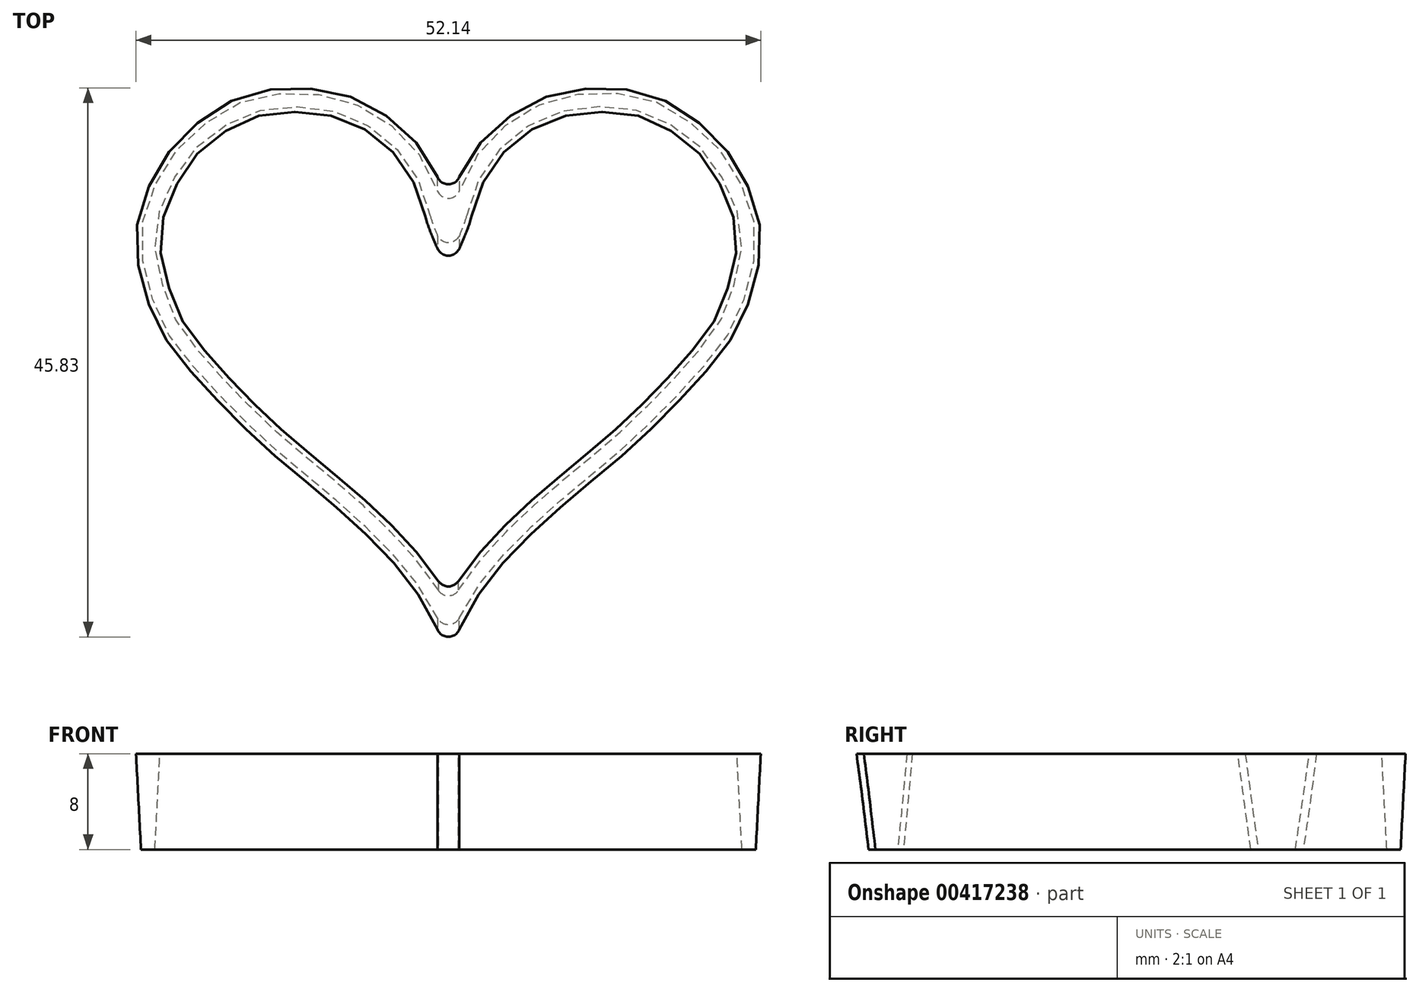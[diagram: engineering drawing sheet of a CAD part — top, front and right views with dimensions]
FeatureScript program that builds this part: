
annotation { "Feature Type Name" : "Feature", "Feature Type Description" : "" }
export const myFeature = defineFeature(function(context is Context, id is Id, definition is map)
    precondition{}
    {
        {
            var Q0;
            Q0=qCreatedBy(makeId("Top.planeOp"),FACE);
            var sketch = newSketch(context, id + "F0", { "sketchPlane" : qUnion([Q0])});
            skLineSegment(sketch, "E0", {"start": v(0, 0) * mm, "end": v(-23.1, 0) * mm, "construction": true});
            skLineSegment(sketch, "E1", {"start": v(0, 0) * mm, "end": v(0, 9) * mm, "construction": true});
            skLineSegment(sketch, "E2", {"start": v(0, 0) * mm, "end": v(0, -25.53) * mm, "construction": true});
            skFitSpline(sketch, "E3", {"points": [v(0, -25.53) * mm, v(-3.22, -19.63) * mm, v(-10.62, -12.4) * mm, v(-15.3, -8.43) * mm, v(-23.1, 0) * mm, v(-24.8, 3.68) * mm, v(-25.64, 8.82) * mm, v(-23.84, 14.09) * mm, v(-21.76, 16.76) * mm, v(-17.5, 19.71) * mm, v(-13.07, 20.55) * mm, v(-8.64, 19.95) * mm, v(-4.57, 17.68) * mm, v(-1.58, 13.97) * mm, v(0, 9) * mm], "startDerivative": vector(-21.33, 67.93) * mm, "endDerivative": vector(17.09, -71.8) * mm});
            skFitSpline(sketch, "E4.MirrorCS", {"points": [v(0, -25.53) * mm, v(3.22, -19.63) * mm, v(10.62, -12.4) * mm, v(15.3, -8.43) * mm, v(23.1, 0) * mm, v(24.8, 3.68) * mm, v(25.64, 8.82) * mm, v(23.84, 14.09) * mm, v(21.76, 16.76) * mm, v(17.5, 19.71) * mm, v(13.07, 20.55) * mm, v(8.64, 19.95) * mm, v(4.57, 17.68) * mm, v(1.58, 13.97) * mm, v(0, 9) * mm], "startDerivative": vector(21.33, 67.93) * mm, "endDerivative": vector(-17.09, -71.8) * mm});
            skSolve(sketch);
        }
        {
            var Q0;
            Q0 = qSketchRegion(id + "F0", true);
            extrude(context, id + "F1", {"entities" : qUnion([Q0]), "depth" : 8 * mm, "hasDraft" : true, "draftAngle" : 3 * degree});
        }
        {
            var Q0;
            Q0=makeQuery(id+"F1.opExtrude","CAP_FACE",FACE,{"disambiguationData":[OSD([sQuery(id+"F0.wireOp",EDGE,"E3"),sQuery(id+"F0.wireOp",EDGE,"E4.MirrorCS")])],"isStart":false});
            var sketch = newSketch(context, id + "F2", { "sketchPlane" : qUnion([Q0])});
            skFitSpline(sketch, "E5.1", {"points": [v(0, -26.93) * mm, v(-0.13, -26.5) * mm, v(-0.27, -26.08) * mm, v(-0.4, -25.65) * mm, v(-0.83, -24.28) * mm, v(-1.54, -22.73) * mm, v(-2.94, -20.7) * mm, v(-3.24, -20.28) * mm, v(-3.9, -19.45) * mm, v(-4.26, -19.02) * mm, v(-5.4, -17.76) * mm, v(-6.23, -16.91) * mm, v(-7.92, -15.3) * mm, v(-8.77, -14.53) * mm, v(-9.97, -13.5) * mm, v(-10.36, -13.16) * mm, v(-11.09, -12.55) * mm, v(-11.43, -12.27) * mm, v(-12.4, -11.47) * mm, v(-13, -11) * mm, v(-14.26, -9.94) * mm, v(-14.92, -9.36) * mm, v(-17.24, -7.21) * mm, v(-19.2, -5.25) * mm, v(-21.72, -2.45) * mm, v(-22.48, -1.54) * mm, v(-23.23, -0.53) * mm, v(-23.38, -0.34) * mm, v(-23.63, 0.04) * mm, v(-23.75, 0.22) * mm, v(-24.08, 0.75) * mm, v(-24.26, 1.08) * mm, v(-24.56, 1.72) * mm, v(-24.7, 2.02) * mm, v(-24.92, 2.64) * mm, v(-25.02, 2.95) * mm, v(-25.17, 3.44) * mm, v(-25.22, 3.6) * mm, v(-25.32, 3.94) * mm, v(-25.37, 4.12) * mm, v(-25.53, 4.66) * mm, v(-25.63, 5.04) * mm, v(-25.9, 6.23) * mm, v(-26.05, 7.09) * mm, v(-26.08, 8.18) * mm, v(-26.08, 8.4) * mm, v(-26.06, 8.85) * mm, v(-26.04, 9.07) * mm, v(-25.96, 9.74) * mm, v(-25.87, 10.17) * mm, v(-25.53, 11.46) * mm, v(-25.2, 12.28) * mm, v(-24.68, 13.4) * mm, v(-24.5, 13.76) * mm, v(-24.14, 14.43) * mm, v(-23.96, 14.74) * mm, v(-23.42, 15.61) * mm, v(-23.04, 16.13) * mm, v(-22.36, 16.89) * mm, v(-22.12, 17.14) * mm, v(-21.58, 17.64) * mm, v(-21.28, 17.88) * mm, v(-20.35, 18.62) * mm, v(-19.65, 19.09) * mm, v(-18.56, 19.7) * mm, v(-18.19, 19.88) * mm, v(-17.44, 20.2) * mm, v(-17.07, 20.33) * mm, v(-15.94, 20.68) * mm, v(-15.2, 20.82) * mm, v(-14.07, 20.93) * mm, v(-13.7, 20.95) * mm, v(-12.95, 20.98) * mm, v(-12.57, 20.98) * mm, v(-11.44, 20.94) * mm, v(-10.68, 20.86) * mm, v(-9.56, 20.64) * mm, v(-9.19, 20.55) * mm, v(-8.45, 20.34) * mm, v(-8.08, 20.21) * mm, v(-7, 19.77) * mm, v(-6.31, 19.4) * mm, v(-5, 18.57) * mm, v(-4.37, 18.09) * mm, v(-3.22, 17.03) * mm, v(-2.69, 16.45) * mm, v(-1.98, 15.49) * mm, v(-1.76, 15.16) * mm, v(-1.36, 14.46) * mm, v(-1.17, 14.1) * mm, v(-0.67, 12.99) * mm, v(-0.4, 12.2) * mm, v(-0.12, 11.2) * mm, v(-0.06, 10.97) * mm, v(0, 10.75) * mm], "construction": true});
            skFitSpline(sketch, "E6.0", {"points": [v(0, -26.93) * mm, v(0.13, -26.5) * mm, v(0.27, -26.08) * mm, v(0.4, -25.65) * mm, v(0.83, -24.28) * mm, v(1.54, -22.73) * mm, v(2.94, -20.7) * mm, v(3.24, -20.28) * mm, v(3.9, -19.45) * mm, v(4.26, -19.02) * mm, v(5.4, -17.76) * mm, v(6.23, -16.91) * mm, v(7.92, -15.3) * mm, v(8.77, -14.53) * mm, v(9.97, -13.5) * mm, v(10.36, -13.16) * mm, v(11.09, -12.55) * mm, v(11.43, -12.27) * mm, v(12.4, -11.47) * mm, v(13, -11) * mm, v(14.26, -9.94) * mm, v(14.92, -9.36) * mm, v(17.24, -7.21) * mm, v(19.2, -5.25) * mm, v(21.72, -2.45) * mm, v(22.48, -1.54) * mm, v(23.23, -0.53) * mm, v(23.38, -0.34) * mm, v(23.63, 0.04) * mm, v(23.75, 0.22) * mm, v(24.08, 0.75) * mm, v(24.26, 1.08) * mm, v(24.56, 1.72) * mm, v(24.7, 2.02) * mm, v(24.92, 2.64) * mm, v(25.02, 2.95) * mm, v(25.17, 3.44) * mm, v(25.22, 3.6) * mm, v(25.32, 3.94) * mm, v(25.37, 4.12) * mm, v(25.53, 4.66) * mm, v(25.63, 5.04) * mm, v(25.9, 6.23) * mm, v(26.05, 7.09) * mm, v(26.08, 8.18) * mm, v(26.08, 8.4) * mm, v(26.06, 8.85) * mm, v(26.04, 9.07) * mm, v(25.96, 9.74) * mm, v(25.87, 10.17) * mm, v(25.53, 11.46) * mm, v(25.2, 12.28) * mm, v(24.68, 13.4) * mm, v(24.5, 13.76) * mm, v(24.14, 14.43) * mm, v(23.96, 14.74) * mm, v(23.42, 15.61) * mm, v(23.04, 16.13) * mm, v(22.36, 16.89) * mm, v(22.12, 17.14) * mm, v(21.58, 17.64) * mm, v(21.28, 17.88) * mm, v(20.35, 18.62) * mm, v(19.65, 19.09) * mm, v(18.56, 19.7) * mm, v(18.19, 19.88) * mm, v(17.44, 20.2) * mm, v(17.07, 20.33) * mm, v(15.94, 20.68) * mm, v(15.2, 20.82) * mm, v(14.07, 20.93) * mm, v(13.7, 20.95) * mm, v(12.95, 20.98) * mm, v(12.57, 20.98) * mm, v(11.44, 20.94) * mm, v(10.68, 20.86) * mm, v(9.56, 20.64) * mm, v(9.19, 20.55) * mm, v(8.45, 20.34) * mm, v(8.08, 20.21) * mm, v(7, 19.77) * mm, v(6.31, 19.4) * mm, v(5, 18.57) * mm, v(4.37, 18.09) * mm, v(3.22, 17.03) * mm, v(2.69, 16.45) * mm, v(1.98, 15.49) * mm, v(1.76, 15.16) * mm, v(1.36, 14.46) * mm, v(1.17, 14.1) * mm, v(0.67, 12.99) * mm, v(0.4, 12.2) * mm, v(0.12, 11.2) * mm, v(0.06, 10.97) * mm, v(0, 10.75) * mm], "construction": true});
            skFitSpline(sketch, "E7.0", {"points": [v(1.9, -26.33) * mm, v(1.85, -26.16) * mm, v(1.77, -25.9) * mm, v(1.67, -25.56) * mm, v(1.6, -25.34) * mm, v(1.55, -25.2) * mm, v(1.52, -25.1) * mm, v(1.5, -25.04) * mm, v(1.48, -24.97) * mm, v(1.45, -24.87) * mm, v(1.4, -24.7) * mm, v(1.3, -24.45) * mm, v(1.16, -24.05) * mm, v(0.96, -23.53) * mm, v(0.59, -22.7) * mm, v(0.04, -21.63) * mm, v(-0.76, -20.31) * mm, v(-1.7, -18.97) * mm, v(-2.83, -17.6) * mm, v(-4.46, -15.83) * mm, v(-6.23, -14.13) * mm, v(-7.94, -12.6) * mm, v(-8.95, -11.74) * mm, v(-9.7, -11.11) * mm, v(-10.39, -10.54) * mm, v(-11.19, -9.89) * mm, v(-12.09, -9.15) * mm, v(-13, -8.38) * mm, v(-13.82, -7.65) * mm, v(-14.56, -6.96) * mm, v(-15.36, -6.21) * mm, v(-16.42, -5.17) * mm, v(-17.74, -3.83) * mm, v(-19.04, -2.45) * mm, v(-20.03, -1.33) * mm, v(-20.74, -0.48) * mm, v(-21.23, 0.12) * mm, v(-21.65, 0.68) * mm, v(-22, 1.18) * mm, v(-22.27, 1.62) * mm, v(-22.57, 2.16) * mm, v(-22.79, 2.65) * mm, v(-22.98, 3.16) * mm, v(-23.11, 3.57) * mm, v(-23.25, 4.03) * mm, v(-23.45, 4.69) * mm, v(-23.7, 5.54) * mm, v(-23.94, 6.6) * mm, v(-24.06, 7.5) * mm, v(-24.08, 8.1) * mm, v(-24.08, 8.45) * mm, v(-24.06, 8.78) * mm, v(-24.01, 9.2) * mm, v(-23.88, 9.9) * mm, v(-23.62, 10.8) * mm, v(-23.2, 11.85) * mm, v(-22.85, 12.6) * mm, v(-22.6, 13.06) * mm, v(-22.44, 13.36) * mm, v(-22.16, 13.85) * mm, v(-21.78, 14.46) * mm, v(-21.3, 15.09) * mm, v(-20.75, 15.68) * mm, v(-20.05, 16.32) * mm, v(-19.21, 16.96) * mm, v(-18.3, 17.56) * mm, v(-17.52, 17.98) * mm, v(-16.9, 18.25) * mm, v(-16.3, 18.48) * mm, v(-15.23, 18.8) * mm, v(-13.98, 18.95) * mm, v(-12.65, 18.98) * mm, v(-11.33, 18.93) * mm, v(-10.04, 18.73) * mm, v(-8.83, 18.37) * mm, v(-7.64, 17.87) * mm, v(-6.5, 17.19) * mm, v(-5.45, 16.37) * mm, v(-4.72, 15.69) * mm, v(-4.07, 14.96) * mm, v(-3.5, 14.16) * mm, v(-3.08, 13.45) * mm, v(-2.8, 12.85) * mm, v(-2.53, 12.2) * mm, v(-2.24, 11.34) * mm, v(-2.03, 10.61) * mm, v(-1.93, 10.24) * mm]});
            skFitSpline(sketch, "E7.1", {"points": [v(-1.9, -26.33) * mm, v(-1.85, -26.16) * mm, v(-1.77, -25.9) * mm, v(-1.67, -25.56) * mm, v(-1.6, -25.34) * mm, v(-1.55, -25.2) * mm, v(-1.52, -25.1) * mm, v(-1.5, -25.04) * mm, v(-1.48, -24.97) * mm, v(-1.45, -24.87) * mm, v(-1.4, -24.7) * mm, v(-1.3, -24.45) * mm, v(-1.16, -24.05) * mm, v(-0.96, -23.53) * mm, v(-0.59, -22.7) * mm, v(-0.04, -21.63) * mm, v(0.76, -20.31) * mm, v(1.7, -18.97) * mm, v(2.83, -17.6) * mm, v(4.46, -15.83) * mm, v(6.23, -14.13) * mm, v(7.94, -12.6) * mm, v(8.95, -11.74) * mm, v(9.7, -11.11) * mm, v(10.39, -10.54) * mm, v(11.19, -9.89) * mm, v(12.09, -9.15) * mm, v(13, -8.38) * mm, v(13.82, -7.65) * mm, v(14.56, -6.96) * mm, v(15.36, -6.21) * mm, v(16.42, -5.17) * mm, v(17.74, -3.83) * mm, v(19.04, -2.45) * mm, v(20.03, -1.33) * mm, v(20.74, -0.48) * mm, v(21.23, 0.12) * mm, v(21.65, 0.68) * mm, v(22, 1.18) * mm, v(22.27, 1.62) * mm, v(22.57, 2.16) * mm, v(22.79, 2.65) * mm, v(22.98, 3.16) * mm, v(23.11, 3.57) * mm, v(23.25, 4.03) * mm, v(23.45, 4.69) * mm, v(23.7, 5.54) * mm, v(23.94, 6.6) * mm, v(24.06, 7.5) * mm, v(24.08, 8.1) * mm, v(24.08, 8.45) * mm, v(24.06, 8.78) * mm, v(24.01, 9.2) * mm, v(23.88, 9.9) * mm, v(23.62, 10.8) * mm, v(23.2, 11.85) * mm, v(22.85, 12.6) * mm, v(22.6, 13.06) * mm, v(22.44, 13.36) * mm, v(22.16, 13.85) * mm, v(21.78, 14.46) * mm, v(21.3, 15.09) * mm, v(20.75, 15.68) * mm, v(20.05, 16.32) * mm, v(19.21, 16.96) * mm, v(18.3, 17.56) * mm, v(17.52, 17.98) * mm, v(16.9, 18.25) * mm, v(16.3, 18.48) * mm, v(15.23, 18.8) * mm, v(13.98, 18.95) * mm, v(12.65, 18.98) * mm, v(11.33, 18.93) * mm, v(10.04, 18.73) * mm, v(8.83, 18.37) * mm, v(7.64, 17.87) * mm, v(6.5, 17.19) * mm, v(5.45, 16.37) * mm, v(4.72, 15.69) * mm, v(4.07, 14.96) * mm, v(3.5, 14.16) * mm, v(3.08, 13.45) * mm, v(2.8, 12.85) * mm, v(2.53, 12.2) * mm, v(2.24, 11.34) * mm, v(2.03, 10.61) * mm, v(1.93, 10.24) * mm]});
            skLineSegment(sketch, "E8", {"start": v(0, 0) * mm, "end": v(0, 10.75) * mm, "construction": true});
            skFitSpline(sketch, "E9", {"points": [v(-1.93, 10.24) * mm, v(0, 4.23) * mm], "startDerivative": vector(1.44, -5.47) * mm, "endDerivative": vector(0, -5.66) * mm});
            skFitSpline(sketch, "E10.MirrorCS", {"points": [v(1.93, 10.24) * mm, v(0, 4.23) * mm], "startDerivative": vector(-1.44, -5.47) * mm, "endDerivative": vector(0, -5.66) * mm});
            skSolve(sketch);
        }
        {
            var Q0;
            Q0 = qSketchRegion(id + "F2", true);
            extrude(context, id + "F3", {"entities" : qUnion([Q0]), "operationType" : NewBodyOperationType.REMOVE, "oppositeDirection" : true, "depth" : 25 * mm, "hasDraft" : true, "draftAngle" : 3 * degree});
        }
        {
            var Q0;
            Q0=makeQuery(id+"F3.boolean.opBoolean","COPY",EDGE,{"derivedFrom":makeQuery(id+"F3.opExtrude","SWEPT_EDGE",EDGE,{"disambiguationData":[OSD([sQuery(id+"F2.wireOp",EDGE,"E9"),sQuery(id+"F2.wireOp",EDGE,"E10.MirrorCS")])]})});
            var Q1;
            {var subQ0=sQuery(id+"F0.wireOp",EDGE,"E4.MirrorCS");var subQ1=sQuery(id+"F0.wireOp",EDGE,"E3");Q1=makeQuery(id+"F1.opExtrude","SWEPT_EDGE",EDGE,{"disambiguationData":[OSD([subQ1,subQ0]),TDD([makeQuery(id+"F0.imprint","INTERSECT",VERTEX,{"disambiguationData":[OD(1.0)],"derivedFrom":[subQ1,subQ0]})])]});}
            var Q2;
            {var subQ0=sQuery(id+"F0.wireOp",EDGE,"E4.MirrorCS");var subQ1=sQuery(id+"F0.wireOp",EDGE,"E3");Q2=makeQuery(id+"F1.opExtrude","SWEPT_EDGE",EDGE,{"disambiguationData":[OSD([subQ1,subQ0]),TDD([makeQuery(id+"F0.imprint","INTERSECT",VERTEX,{"disambiguationData":[OD(0.0)],"derivedFrom":[subQ1,subQ0]})])]});}
            var Q3;
            Q3=makeQuery(id+"F3.boolean.opBoolean","COPY",EDGE,{"derivedFrom":makeQuery(id+"F3.opExtrude","SWEPT_EDGE",EDGE,{"disambiguationData":[OSD([sQuery(id+"F2.wireOp",EDGE,"E7.0"),sQuery(id+"F2.wireOp",EDGE,"E7.1")])]})});
            fillet(context, id + "F4", {"entities" : qUnion([Q0, Q1, Q2, Q3]), "radius" : 1 * mm, "tangentPropagation" : true, "allowEdgeOverflow" : false});
        }
        {
            var Q0;
            Q0=makeQuery(id+"F1.opExtrude","CAP_FACE",FACE,{"disambiguationData":[OSD([sQuery(id+"F0.wireOp",EDGE,"E3"),sQuery(id+"F0.wireOp",EDGE,"E4.MirrorCS")])],"isStart":false});
            cPlane(context, id + "F5", {"entities" : qUnion([Q0]), "cplaneType" : CPlaneType.OFFSET, "offset" : 4 * mm, "oppositeDirection" : true, "width" : 150 * mm, "height" : 150 * mm});
        }
    });
